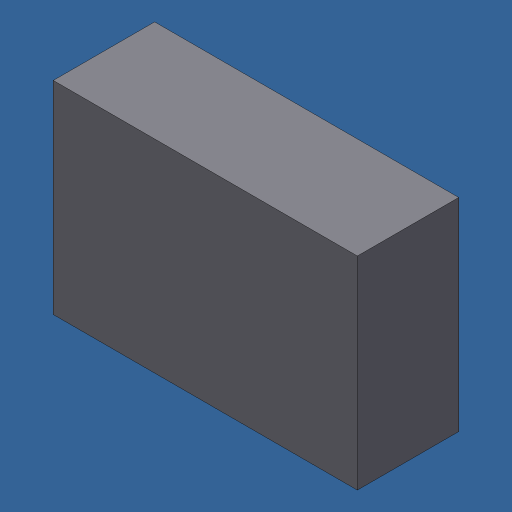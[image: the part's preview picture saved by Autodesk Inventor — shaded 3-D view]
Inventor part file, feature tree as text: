
AUTODESK INVENTOR PART (.ipt)
format: ipt  version: 2024.3 (Build 283343000, 343)  size: 108,544 bytes
history: native  units: mm
features: other x1, extrude x1
ambient origin geometry x8: Origin, YZ Plane, XZ Plane, XY Plane, X Axis, Y Axis, Z Axis, Center Point
bodies: Body1 (feature_tree)
feature tree (2):
  other  "Finish - None"
  extrude  "Extrusion1"  TaperAngle=0.0deg  [1 undecoded]
note: 1 required parameter value undecoded (feature->parameter linkage not recoverable at this tier; creation-order binding heuristic only, values carry confidence <= 0.55)
